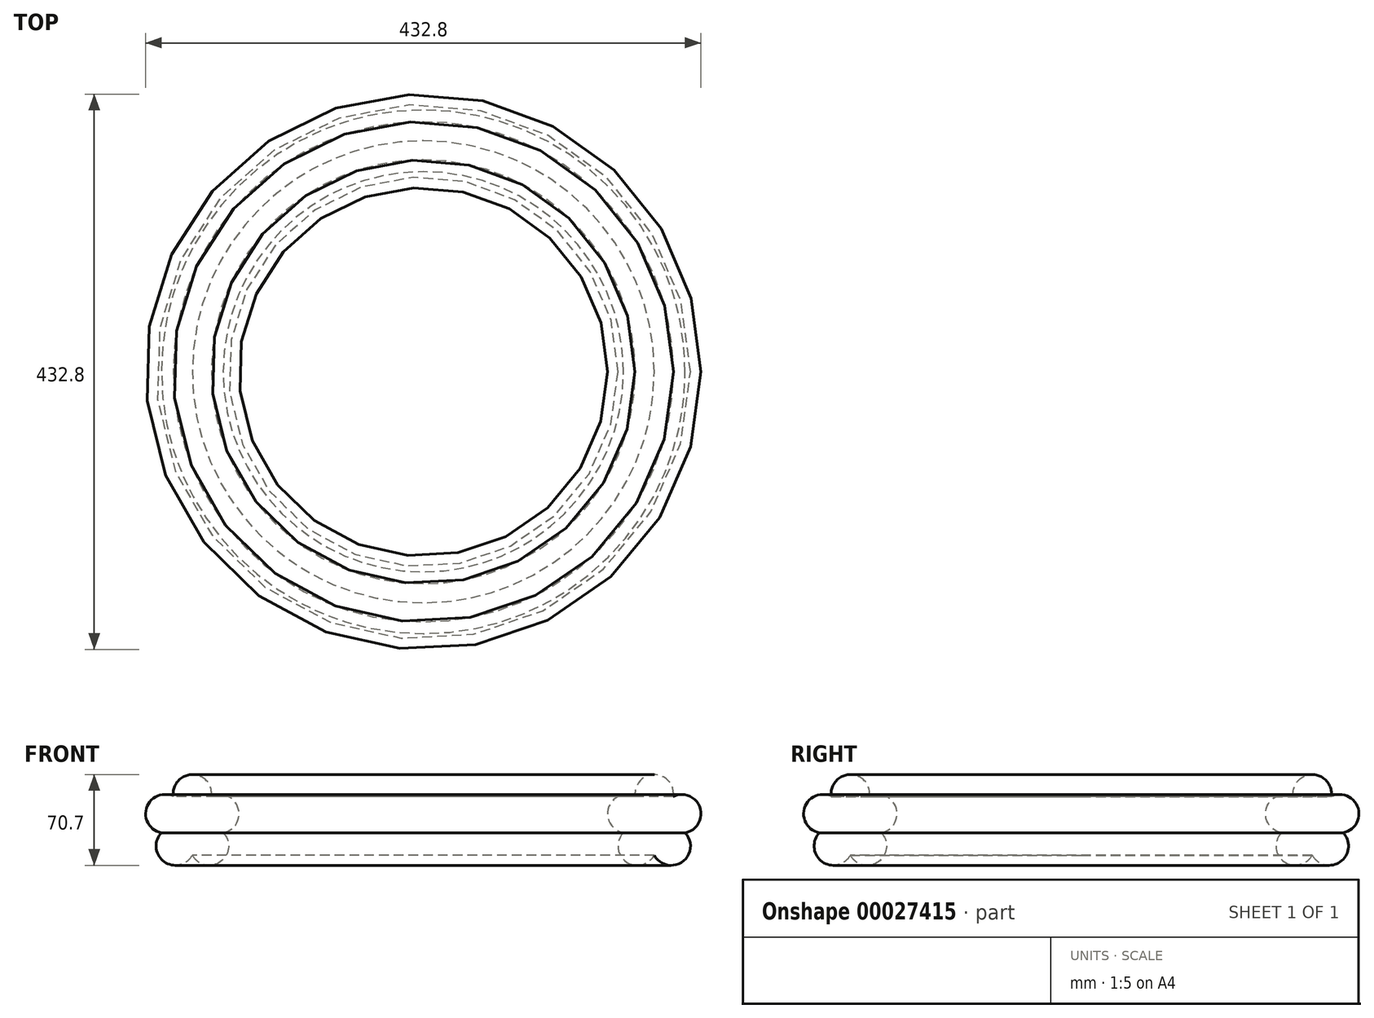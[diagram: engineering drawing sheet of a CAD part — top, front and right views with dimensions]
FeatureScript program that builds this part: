
annotation { "Feature Type Name" : "Feature", "Feature Type Description" : "" }
export const myFeature = defineFeature(function(context is Context, id is Id, definition is map)
    precondition{}
    {
        {
            var Q0;
            Q0=qCreatedBy(makeId("Front.planeOp"),FACE);
            var sketch = newSketch(context, id + "F0", { "sketchPlane" : qUnion([Q0])});
            skCircle(sketch, "E0", {"center": v(0, 0) * mm, "radius": 22.5 * mm, "construction": true});
            skLineSegment(sketch, "E1", {"start": v(0, 0) * mm, "end": v(0, 22.5) * mm, "construction": true});
            skArc(sketch, "E2", {"start": v(14.86, 20.45) * mm, "mid": v(0, 37.5) * mm, "end": v(-14.86, 20.45) * mm});
            skArc(sketch, "E3.1.0", {"start": v(-14.86, 20.45) * mm, "mid": v(-35.66, 11.59) * mm, "end": v(-24.04, -7.81) * mm});
            skArc(sketch, "E3.2.0", {"start": v(-24.04, -7.81) * mm, "mid": v(-22.04, -30.34) * mm, "end": v(0, -25.28) * mm});
            skArc(sketch, "E3.3.0", {"start": v(0, -25.28) * mm, "mid": v(22.04, -30.34) * mm, "end": v(24.04, -7.81) * mm});
            skArc(sketch, "E3.4.0", {"start": v(24.04, -7.81) * mm, "mid": v(35.66, 11.59) * mm, "end": v(14.86, 20.45) * mm});
            skSolve(sketch);
        }
        {
            var Q0;
            Q0=qCreatedBy(makeId("Front.planeOp"),FACE);
            var sketch = newSketch(context, id + "F1", { "sketchPlane" : qUnion([Q0])});
            skLineSegment(sketch, "E4", {"start": v(0, 0) * mm, "end": v(-180, 0) * mm, "construction": true});
            skLineSegment(sketch, "E5", {"start": v(-180, 143.67) * mm, "end": v(-180, -95.14) * mm, "construction": true});
            skSolve(sketch);
        }
        {
            var Q0;
            Q0=makeQuery(id+"F0.imprint","IMPRINT",FACE,{"disambiguationData":[TD([[makeQuery(id+"F0.imprint","IMPRINT",EDGE,{"derivedFrom":sQuery(id+"F0.wireOp",EDGE,"E2")}),1.0]])]});
            var Q1;
            Q1=sQuery(id+"F1.wireOp",EDGE,"E5");
            revolve(context, id + "F2", {"entities" : qUnion([Q0]), "axis" : qUnion([Q1]), "revolveType" : RevolveType.FULL});
        }
    });
